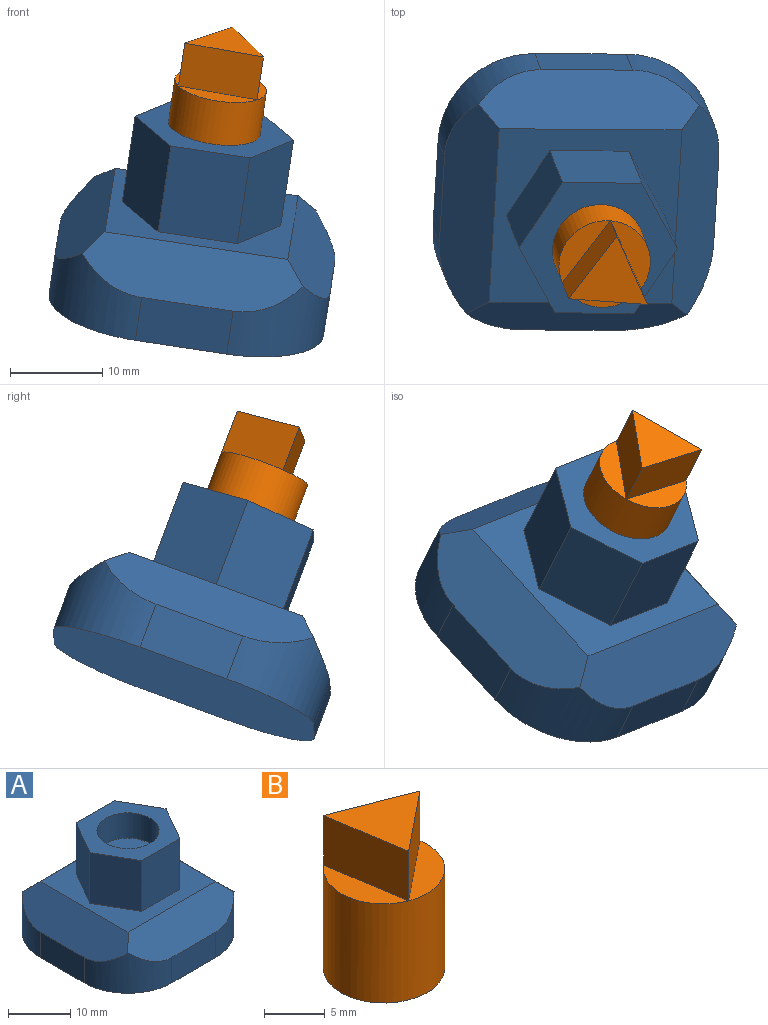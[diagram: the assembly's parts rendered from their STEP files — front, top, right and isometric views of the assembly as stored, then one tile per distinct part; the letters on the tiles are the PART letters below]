
ASSEMBLY  parts=2 mates=1
PART A: 23 faces, bbox 30x30x20 mm
  f0: plane 20x20mm, normal (0,0,1), area 205.1mm2, adj f6,f7,f8,f9,f10,f11,f13,f14
  f1: plane 10x5mm, normal (0,1,0), area 50mm2, adj f5,f14,f19,f21
  f2: plane 10x5mm, normal (-1,0,0), area 50mm2, adj f5,f16,f21,f22
  f3: plane 10x5mm, normal (0,-1,0), area 50mm2, adj f5,f15,f20,f22
  f4: plane 10x5mm, normal (1,0,0), area 50mm2, adj f5,f13,f19,f20
  f5: plane 30x30mm, normal (0,0,-1), area 814.2mm2, adj f1,f2,f3,f4,f19,f20,f21,f22
  f6: plane 10x8.66mm, normal (0,-1,0), area 86.6mm2, adj f0,f7,f11,f12
  f7: plane 10x7.5mm, normal (0.87,-0.5,0), area 86.6mm2, adj f0,f6,f8,f12
  f8: plane 10x7.5mm, normal (0.87,0.5,0), area 86.6mm2, adj f0,f7,f9,f12
  f9: plane 10x8.66mm, normal (0,1,0), area 86.6mm2, adj f0,f8,f10,f12
  f10: plane 10x7.5mm, normal (-0.87,0.5,0), area 86.6mm2, adj f0,f9,f11,f12
  f11: plane 10x7.5mm, normal (-0.87,-0.5,0), area 86.6mm2, adj f0,f6,f10,f12
  f12: plane 17.32x15mm, normal (0,0,1), area 116.3mm2, adj f6,f7,f8,f9,f10,f11,f17
  f13: plane 24.14x5mm, normal (0.71,0,0.71), area 146.4mm2, adj f0,f4,f14,f15,f19,f20
  f14: plane 24.14x5mm, normal (0,0.71,0.71), area 146.4mm2, adj f0,f1,f13,f16,f19,f21
  f15: plane 24.14x5mm, normal (0,-0.71,0.71), area 146.4mm2, adj f0,f3,f13,f16,f20,f22
  f16: plane 24.14x5mm, normal (-0.71,0,0.71), area 146.4mm2, adj f0,f2,f14,f15,f21,f22
  f17: cylinder r=5mm len=10mm, axis (0,0,1), area 157.1mm2, adj f12,f18
  f18: plane 10x10mm, normal (0,0,1), area 78.5mm2, adj f17
  f19: cylinder r=10mm len=10mm, axis (0,0,-1), area 94.2mm2, adj f1,f4,f5,f13,f14
  f20: cylinder r=10mm len=10mm, axis (0,0,1), area 94.2mm2, adj f3,f4,f5,f13,f15
  f21: cylinder r=10mm len=10mm, axis (0,0,1), area 94.2mm2, adj f1,f2,f5,f14,f16
  f22: cylinder r=10mm len=10mm, axis (0,0,-1), area 94.2mm2, adj f2,f3,f5,f15,f16
PART B: 9 faces, bbox 10x10x15 mm
  f0: plane 8.08x4.23mm, normal (0,0,1), area 15.4mm2, adj f3,f5
  f1: plane 6.8x5.77mm, normal (0,0,1), area 15.4mm2, adj f3,f7
  f2: plane 8.56x3.2mm, normal (0,0,1), area 15.4mm2, adj f3,f6
  f3: cylinder r=5mm len=10mm, axis (0,0,-1), area 314.2mm2, adj f0,f1,f2,f4
  f4: plane 10x10mm, normal (0,0,-1), area 78.5mm2, adj f3
  f5: plane 8.08x5mm, normal (0.36,0.93,0), area 43.3mm2, adj f0,f6,f7,f8
  f6: plane 8.56x5mm, normal (-0.99,-0.15,0), area 43.3mm2, adj f2,f5,f7,f8
  f7: plane 6.74x5.43mm, normal (0.63,-0.78,0), area 43.3mm2, adj f1,f5,f6,f8
  f8: plane 8.56x8.08mm, normal (0,0,1), area 32.5mm2, adj f5,f6,f7
PLACE A rot(axis=(0.92,0.38,-0.08),22deg) t=(-12.95,40.95,-13.96)mm
PLACE B rot(axis=(0.33,0.32,-0.89),49.6deg) t=(-10.87,35.74,-0.05)mm
MATE revolute B.f3 <-> A.f17  axis (-0.14,0.35,-0.93) through (-10.87,35.74,-0.05)mm
